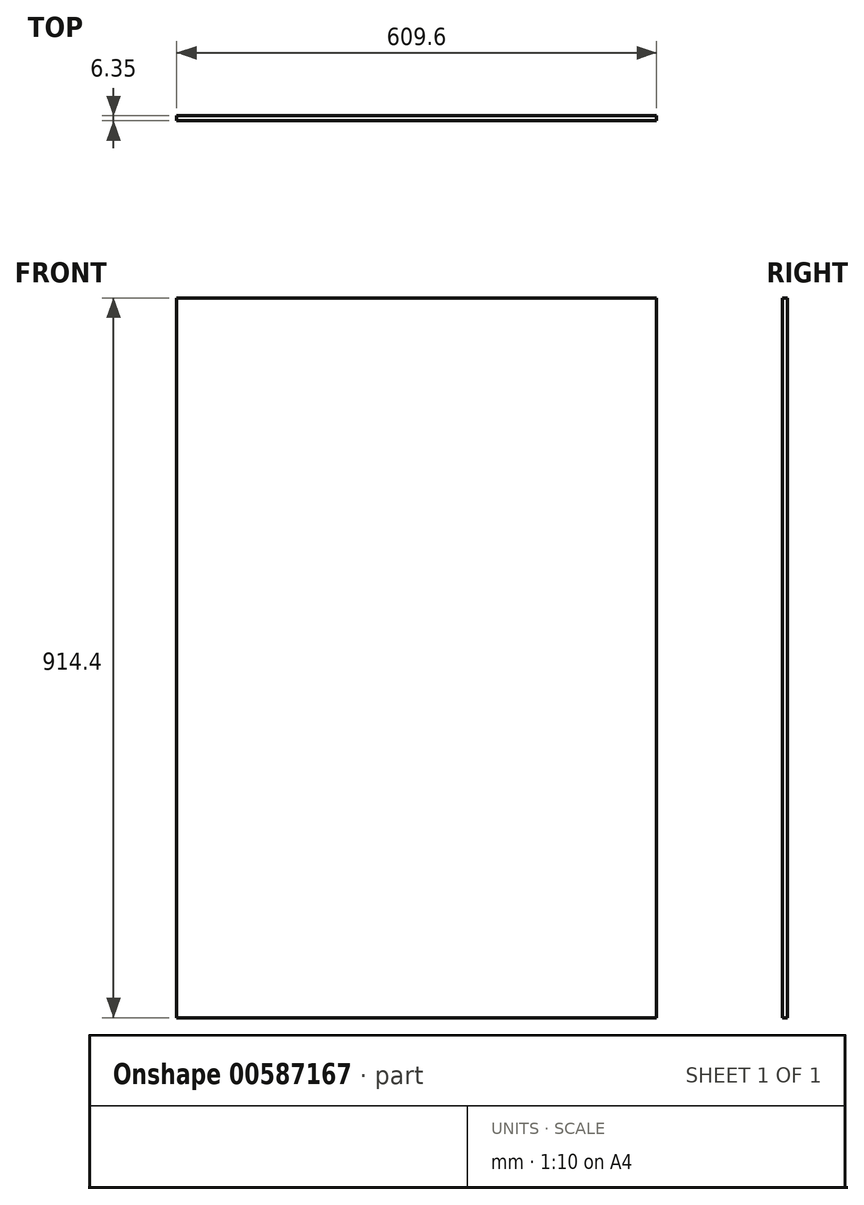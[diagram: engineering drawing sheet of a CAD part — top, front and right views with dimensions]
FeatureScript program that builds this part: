
annotation { "Feature Type Name" : "Feature", "Feature Type Description" : "" }
export const myFeature = defineFeature(function(context is Context, id is Id, definition is map)
    precondition{}
    {
        {
            var Q0;
            Q0=qCreatedBy(makeId("Front.planeOp"),FACE);
            var sketch = newSketch(context, id + "F0", { "sketchPlane" : qUnion([Q0])});
            skLineSegment(sketch, "E0.bottom", {"start": v(-304.8, 457.2) * mm, "end": v(304.8, 457.2) * mm});
            skLineSegment(sketch, "E0.top", {"start": v(-304.8, -457.2) * mm, "end": v(304.8, -457.2) * mm});
            skLineSegment(sketch, "E0.left", {"start": v(-304.8, 457.2) * mm, "end": v(-304.8, -457.2) * mm});
            skLineSegment(sketch, "E0.right", {"start": v(304.8, 457.2) * mm, "end": v(304.8, -457.2) * mm});
            skSolve(sketch);
        }
        {
            var Q0;
            Q0 = qSketchRegion(id + "F0", true);
            extrude(context, id + "F1", {"entities" : qUnion([Q0]), "depth" : 6.35 * mm, "offsetDistance" : 25.4 * mm});
        }
    });
